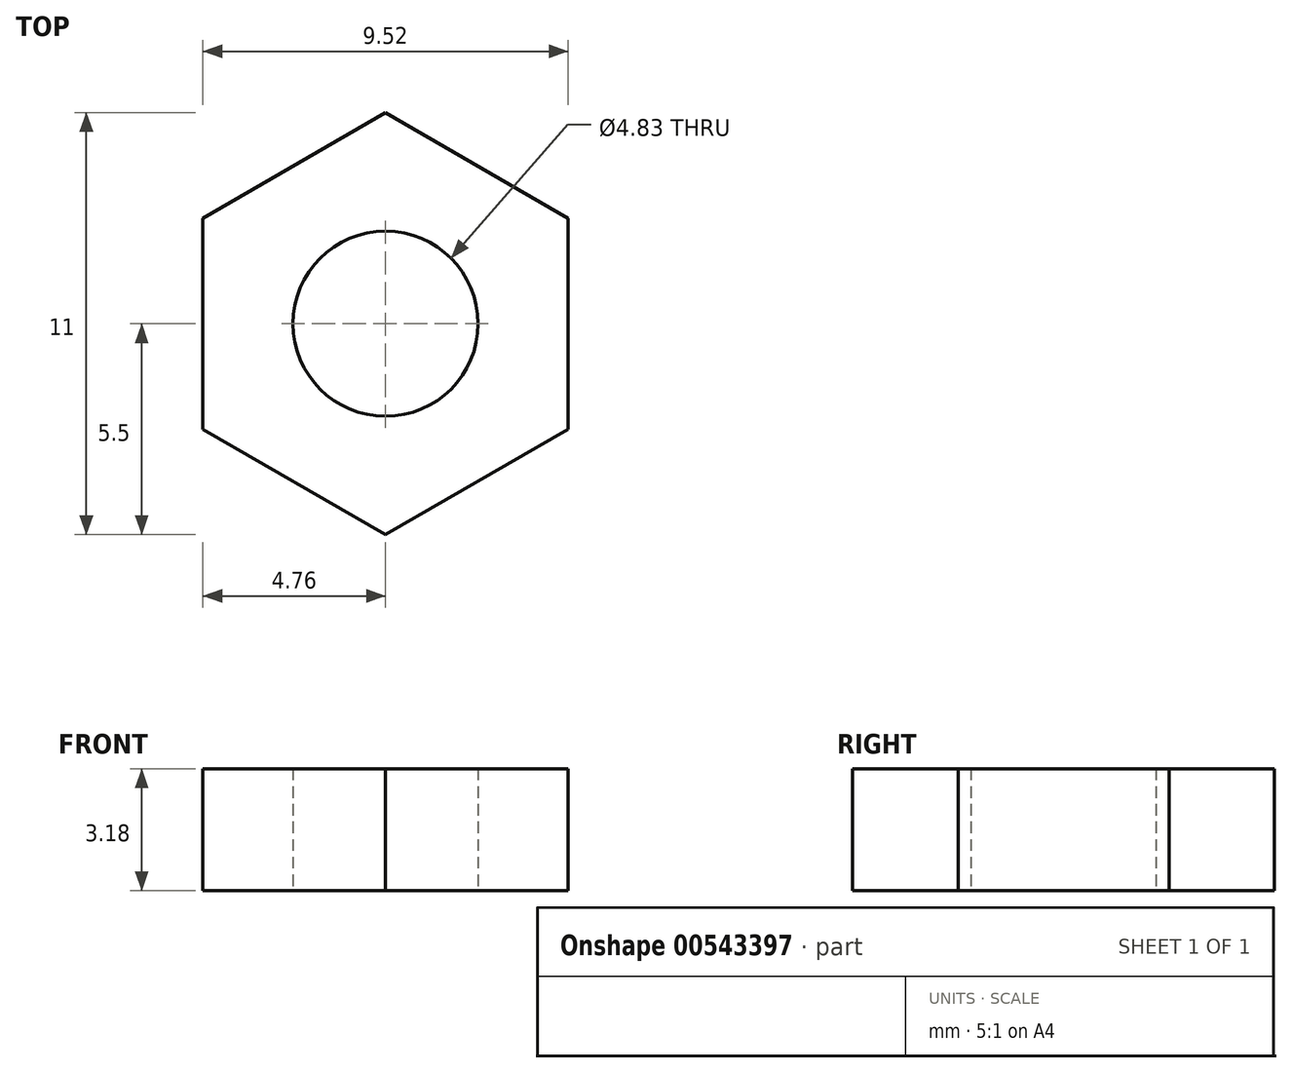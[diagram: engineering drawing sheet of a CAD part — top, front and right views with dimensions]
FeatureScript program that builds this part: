
annotation { "Feature Type Name" : "Feature", "Feature Type Description" : "" }
export const myFeature = defineFeature(function(context is Context, id is Id, definition is map)
    precondition{}
    {
        {
            var Q0;
            Q0=qCreatedBy(makeId("Top.planeOp"),FACE);
            var sketch = newSketch(context, id + "F0", { "sketchPlane" : qUnion([Q0])});
            skCircle(sketch, "E0.cCircle", {"center": v(0, 0) * mm, "radius": 4.76 * mm, "construction": true});
            skLineSegment(sketch, "E0.0", {"start": v(4.76, 2.75) * mm, "end": v(4.76, -2.75) * mm});
            skLineSegment(sketch, "E0.1", {"start": v(4.76, -2.75) * mm, "end": v(0, -5.5) * mm});
            skLineSegment(sketch, "E0.2", {"start": v(0, -5.5) * mm, "end": v(-4.76, -2.75) * mm});
            skLineSegment(sketch, "E0.3", {"start": v(-4.76, -2.75) * mm, "end": v(-4.76, 2.75) * mm});
            skLineSegment(sketch, "E0.4", {"start": v(-4.76, 2.75) * mm, "end": v(0, 5.5) * mm});
            skLineSegment(sketch, "E0.5", {"start": v(0, 5.5) * mm, "end": v(4.76, 2.75) * mm});
            skPoint(sketch, "E0.0.midPoint", {"position": v(4.76, 0) * mm});
            skCircle(sketch, "E1", {"center": v(0, 0) * mm, "radius": 2.41 * mm});
            skSolve(sketch);
        }
        {
            var Q0;
            Q0 = qSketchRegion(id + "F0", true);
            extrude(context, id + "F1", {"entities" : qUnion([Q0]), "endBound" : BoundingType.SYMMETRIC, "depth" : 3.17 * mm, "offsetDistance" : 25.4 * mm});
        }
    });
